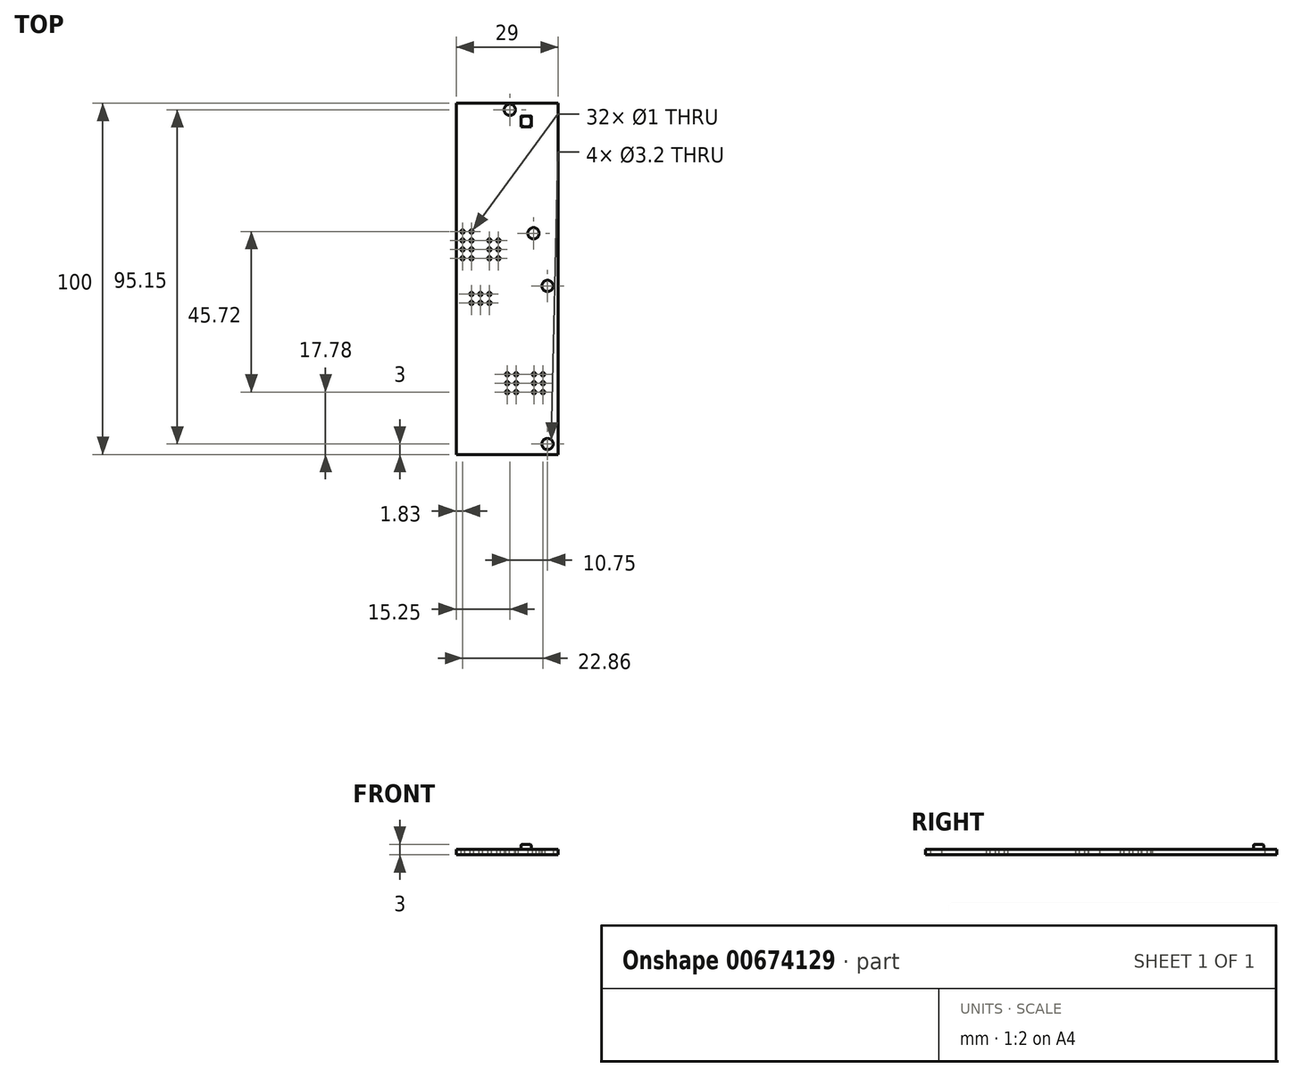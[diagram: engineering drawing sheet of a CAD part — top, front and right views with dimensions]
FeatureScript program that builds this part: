
annotation { "Feature Type Name" : "Feature", "Feature Type Description" : "" }
export const myFeature = defineFeature(function(context is Context, id is Id, definition is map)
    precondition{}
    {
        {
            var Q0;
            Q0=qCreatedBy(makeId("Top.planeOp"),FACE);
            var sketch = newSketch(context, id + "F0", { "sketchPlane" : qUnion([Q0])});
            skLineSegment(sketch, "E0.bottom", {"start": v(14.5, 50) * mm, "end": v(-14.5, 50) * mm});
            skLineSegment(sketch, "E0.top", {"start": v(14.5, -50) * mm, "end": v(-14.5, -50) * mm});
            skLineSegment(sketch, "E0.left", {"start": v(14.5, 50) * mm, "end": v(14.5, -50) * mm});
            skLineSegment(sketch, "E0.right", {"start": v(-14.5, 50) * mm, "end": v(-14.5, -50) * mm});
            skPoint(sketch, "E0.middle", {"position": v(0, 0) * mm});
            skCircle(sketch, "E1", {"center": v(11.5, -47) * mm, "radius": 1.6 * mm});
            skCircle(sketch, "E2", {"center": v(11.5, -2) * mm, "radius": 1.6 * mm});
            skLineSegment(sketch, "E3", {"start": v(14.5, -50) * mm, "end": v(7.25, -50) * mm});
            skLineSegment(sketch, "E4", {"start": v(7.25, -50) * mm, "end": v(-2.65, -50) * mm});
            skCircle(sketch, "E5", {"center": v(7.5, 13) * mm, "radius": 1.6 * mm});
            skCircle(sketch, "E6", {"center": v(0.75, 48.15) * mm, "radius": 1.6 * mm});
            skCircle(sketch, "E7", {"center": v(10.2, -32.22) * mm, "radius": 0.5 * mm});
            skCircle(sketch, "E8.0.1.0", {"center": v(10.2, -29.68) * mm, "radius": 0.5 * mm});
            skCircle(sketch, "E8.0.2.0", {"center": v(10.2, -27.14) * mm, "radius": 0.5 * mm});
            skCircle(sketch, "E8.1.0.0", {"center": v(7.65, -32.22) * mm, "radius": 0.5 * mm});
            skCircle(sketch, "E8.1.1.0", {"center": v(7.65, -29.68) * mm, "radius": 0.5 * mm});
            skCircle(sketch, "E8.1.2.0", {"center": v(7.65, -27.14) * mm, "radius": 0.5 * mm});
            skLineSegment(sketch, "E8.direction1", {"start": v(10.2, -32.22) * mm, "end": v(7.65, -32.22) * mm, "construction": true});
            skLineSegment(sketch, "E8.direction2", {"start": v(10.2, -32.22) * mm, "end": v(10.2, -29.68) * mm, "construction": true});
            skCircle(sketch, "E9", {"center": v(2.57, -32.22) * mm, "radius": 0.5 * mm});
            skCircle(sketch, "E10.0.1.0", {"center": v(2.57, -29.68) * mm, "radius": 0.5 * mm});
            skCircle(sketch, "E10.0.2.0", {"center": v(2.57, -27.14) * mm, "radius": 0.5 * mm});
            skCircle(sketch, "E10.1.0.0", {"center": v(0.03, -32.22) * mm, "radius": 0.5 * mm});
            skCircle(sketch, "E10.1.1.0", {"center": v(0.03, -29.68) * mm, "radius": 0.5 * mm});
            skCircle(sketch, "E10.1.2.0", {"center": v(0.03, -27.14) * mm, "radius": 0.5 * mm});
            skLineSegment(sketch, "E10.direction1", {"start": v(2.57, -32.22) * mm, "end": v(0.03, -32.22) * mm, "construction": true});
            skLineSegment(sketch, "E10.direction2", {"start": v(2.57, -32.22) * mm, "end": v(2.57, -29.68) * mm, "construction": true});
            skCircle(sketch, "E11", {"center": v(-10.13, -6.82) * mm, "radius": 0.5 * mm});
            skCircle(sketch, "E12.0.1.0", {"center": v(-10.13, -4.28) * mm, "radius": 0.5 * mm});
            skCircle(sketch, "E12.1.0.0", {"center": v(-7.59, -6.82) * mm, "radius": 0.5 * mm});
            skCircle(sketch, "E12.1.1.0", {"center": v(-7.59, -4.28) * mm, "radius": 0.5 * mm});
            skCircle(sketch, "E12.2.0.0", {"center": v(-5.05, -6.82) * mm, "radius": 0.5 * mm});
            skCircle(sketch, "E12.2.1.0", {"center": v(-5.05, -4.28) * mm, "radius": 0.5 * mm});
            skLineSegment(sketch, "E12.direction1", {"start": v(-10.13, -6.82) * mm, "end": v(-7.59, -6.82) * mm, "construction": true});
            skLineSegment(sketch, "E12.direction2", {"start": v(-10.13, -6.82) * mm, "end": v(-10.13, -4.28) * mm, "construction": true});
            skCircle(sketch, "E13.2.0.0", {"center": v(-12.67, 5.88) * mm, "radius": 0.5 * mm});
            skCircle(sketch, "E14.0.1.0", {"center": v(-12.67, 8.42) * mm, "radius": 0.5 * mm});
            skCircle(sketch, "E14.0.2.0", {"center": v(-12.67, 10.96) * mm, "radius": 0.5 * mm});
            skCircle(sketch, "E14.0.3.0", {"center": v(-12.67, 13.5) * mm, "radius": 0.5 * mm});
            skCircle(sketch, "E14.1.0.0", {"center": v(-10.13, 5.88) * mm, "radius": 0.5 * mm});
            skCircle(sketch, "E14.1.1.0", {"center": v(-10.13, 8.42) * mm, "radius": 0.5 * mm});
            skCircle(sketch, "E14.1.2.0", {"center": v(-10.13, 10.96) * mm, "radius": 0.5 * mm});
            skCircle(sketch, "E14.1.3.0", {"center": v(-10.13, 13.5) * mm, "radius": 0.5 * mm});
            skLineSegment(sketch, "E14.direction1", {"start": v(-12.67, 5.88) * mm, "end": v(-10.13, 5.88) * mm, "construction": true});
            skLineSegment(sketch, "E14.direction2", {"start": v(-12.67, 5.88) * mm, "end": v(-12.67, 8.42) * mm, "construction": true});
            skCircle(sketch, "E15.1.0.0", {"center": v(-5.05, 5.88) * mm, "radius": 0.5 * mm});
            skCircle(sketch, "E16.0.1.0", {"center": v(-5.05, 8.42) * mm, "radius": 0.5 * mm});
            skCircle(sketch, "E16.0.2.0", {"center": v(-5.05, 10.96) * mm, "radius": 0.5 * mm});
            skCircle(sketch, "E16.1.0.0", {"center": v(-2.5, 5.88) * mm, "radius": 0.5 * mm});
            skCircle(sketch, "E16.1.1.0", {"center": v(-2.5, 8.42) * mm, "radius": 0.5 * mm});
            skCircle(sketch, "E16.1.2.0", {"center": v(-2.5, 10.96) * mm, "radius": 0.5 * mm});
            skLineSegment(sketch, "E16.direction1", {"start": v(-5.05, 5.88) * mm, "end": v(-2.5, 5.88) * mm, "construction": true});
            skLineSegment(sketch, "E16.direction2", {"start": v(-5.05, 5.88) * mm, "end": v(-5.05, 8.42) * mm, "construction": true});
            skLineSegment(sketch, "E17.bottom", {"start": v(6.91, 46.33) * mm, "end": v(3.91, 46.33) * mm});
            skLineSegment(sketch, "E17.top", {"start": v(6.91, 43.33) * mm, "end": v(3.91, 43.33) * mm});
            skLineSegment(sketch, "E17.left", {"start": v(6.91, 46.33) * mm, "end": v(6.91, 43.33) * mm});
            skLineSegment(sketch, "E17.right", {"start": v(3.91, 46.33) * mm, "end": v(3.91, 43.33) * mm});
            skPoint(sketch, "E17.middle", {"position": v(5.41, 44.83) * mm});
            skSolve(sketch);
        }
        {
            var Q0;
            Q0 = qSketchRegion(id + "F0", true);
            var Q1;
            Q1=makeQuery(id+"F0.imprint","IMPRINT",FACE,{"disambiguationData":[TD([[makeQuery(id+"F0.imprint","IMPRINT",EDGE,{"derivedFrom":sQuery(id+"F0.wireOp",EDGE,"E17.bottom")}),1.0]])]});
            extrude(context, id + "F1", {"entities" : qUnion([Q0, Q1]), "depth" : 1.63 * mm, "offsetDistance" : 25 * mm});
        }
        {
            var Q0;
            Q0=makeQuery(id+"F0.imprint","IMPRINT",FACE,{"disambiguationData":[TD([[makeQuery(id+"F0.imprint","IMPRINT",EDGE,{"derivedFrom":sQuery(id+"F0.wireOp",EDGE,"E17.bottom")}),1.0]])]});
            extrude(context, id + "F2", {"entities" : qUnion([Q0]), "operationType" : NewBodyOperationType.ADD, "depth" : 3 * mm, "offsetDistance" : 25 * mm});
        }
        {
            var Q0;
            Q0=makeQuery(id+"F2.opExtrude","CAP_FACE",FACE,{"disambiguationData":[OSD([sQuery(id+"F0.wireOp",EDGE,"E17.bottom"),sQuery(id+"F0.wireOp",EDGE,"E17.top"),sQuery(id+"F0.wireOp",EDGE,"E17.left"),sQuery(id+"F0.wireOp",EDGE,"E17.right")])],"isStart":false});
            fillet(context, id + "F3", {"entities" : qUnion([Q0]), "radius" : 0.5 * mm, "tangentPropagation" : true, "allowEdgeOverflow" : false});
        }
    });
